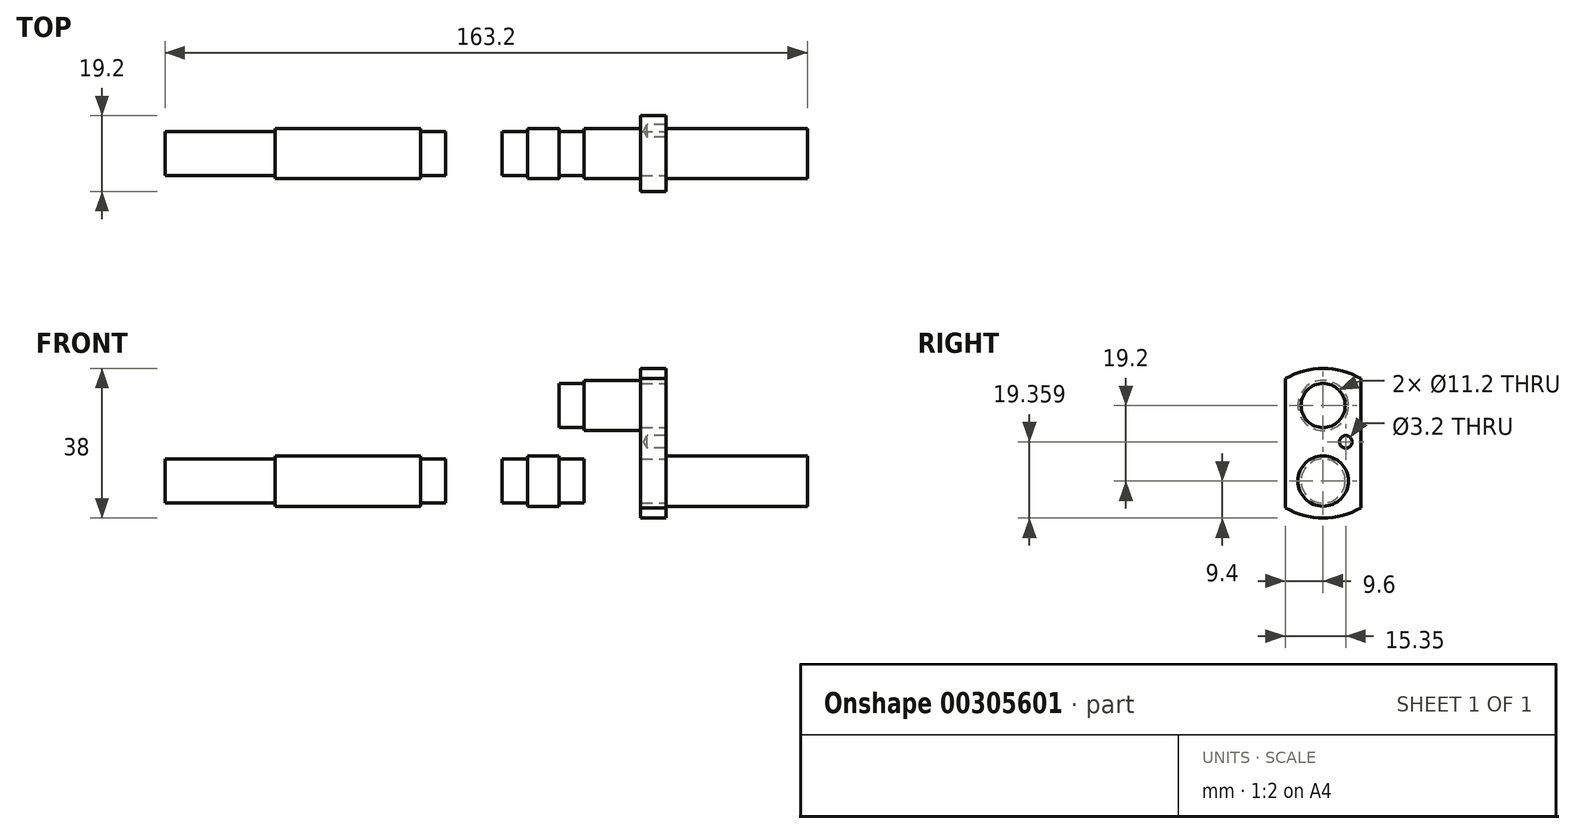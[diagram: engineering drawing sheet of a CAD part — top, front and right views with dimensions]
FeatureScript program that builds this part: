
annotation { "Feature Type Name" : "Feature", "Feature Type Description" : "" }
export const myFeature = defineFeature(function(context is Context, id is Id, definition is map)
    precondition{}
    {
        {
            var Q0;
            Q0=qCreatedBy(makeId("Front.planeOp"),FACE);
            var sketch = newSketch(context, id + "F0", { "sketchPlane" : qUnion([Q0]), "disableImprinting" : false});
            skLineSegment(sketch, "E0", {"start": v(97.03, 0) * mm, "end": v(-113.51, 0) * mm, "construction": true});
            skLineSegment(sketch, "E1", {"start": v(0, 41.9) * mm, "end": v(0, 0) * mm, "construction": true});
            skLineSegment(sketch, "E2", {"start": v(35.2, 41.9) * mm, "end": v(35.2, 0) * mm, "construction": true});
            skLineSegment(sketch, "E3", {"start": v(7.2, 0) * mm, "end": v(7.2, -28.31) * mm, "construction": true});
            skLineSegment(sketch, "E4", {"start": v(13.6, 0) * mm, "end": v(13.6, -28.31) * mm, "construction": true});
            skLineSegment(sketch, "E5", {"start": v(-7.2, 0) * mm, "end": v(-7.2, -28.31) * mm, "construction": true});
            skLineSegment(sketch, "E6", {"start": v(-13.6, 0) * mm, "end": v(-13.6, -28.31) * mm, "construction": true});
            skLineSegment(sketch, "E7", {"start": v(21.6, 0) * mm, "end": v(21.6, -28.31) * mm, "construction": true});
            skLineSegment(sketch, "E8", {"start": v(28, 0) * mm, "end": v(28, -28.31) * mm, "construction": true});
            skLineSegment(sketch, "E9", {"start": v(42.4, 0) * mm, "end": v(42.4, -28.31) * mm, "construction": true});
            skLineSegment(sketch, "E10", {"start": v(42.4, -28.31) * mm, "end": v(48.8, -28.31) * mm, "construction": true});
            skLineSegment(sketch, "E11", {"start": v(48.8, -28.31) * mm, "end": v(48.8, 0) * mm, "construction": true});
            skLineSegment(sketch, "E12", {"start": v(28, -28.31) * mm, "end": v(21.6, -28.31) * mm, "construction": true});
            skLineSegment(sketch, "E13", {"start": v(13.6, -28.31) * mm, "end": v(7.2, -28.31) * mm, "construction": true});
            skLineSegment(sketch, "E14", {"start": v(-7.2, -28.31) * mm, "end": v(-13.6, -28.31) * mm, "construction": true});
            skLineSegment(sketch, "E15", {"start": v(61.58, 19.2) * mm, "end": v(16.8, 19.2) * mm, "construction": true});
            skLineSegment(sketch, "E16", {"start": v(48.8, -6.4) * mm, "end": v(84.7, -6.4) * mm});
            skLineSegment(sketch, "E17", {"start": v(84.7, -6.4) * mm, "end": v(84.7, 0) * mm});
            skLineSegment(sketch, "E18", {"start": v(84.7, 0) * mm, "end": v(42.4, 0) * mm});
            skLineSegment(sketch, "E19", {"start": v(48.8, -6.4) * mm, "end": v(48.8, -5.6) * mm});
            skLineSegment(sketch, "E20", {"start": v(48.8, -5.6) * mm, "end": v(42.4, -5.6) * mm});
            skLineSegment(sketch, "E21", {"start": v(42.4, -5.6) * mm, "end": v(42.4, 0) * mm});
            skLineSegment(sketch, "E22", {"start": v(28, 0) * mm, "end": v(7.2, 0) * mm});
            skLineSegment(sketch, "E23", {"start": v(7.2, -5.6) * mm, "end": v(13.6, -5.6) * mm});
            skLineSegment(sketch, "E24", {"start": v(13.6, -5.6) * mm, "end": v(13.6, -6.4) * mm});
            skLineSegment(sketch, "E25", {"start": v(13.6, -6.4) * mm, "end": v(21.6, -6.4) * mm});
            skLineSegment(sketch, "E26", {"start": v(21.6, -6.4) * mm, "end": v(21.6, -5.6) * mm});
            skLineSegment(sketch, "E27", {"start": v(21.6, -5.6) * mm, "end": v(28, -5.6) * mm});
            skLineSegment(sketch, "E28", {"start": v(28, -5.6) * mm, "end": v(28, 0) * mm});
            skLineSegment(sketch, "E29", {"start": v(7.2, 0) * mm, "end": v(7.2, -5.6) * mm});
            skLineSegment(sketch, "E30", {"start": v(-7.2, 0) * mm, "end": v(-7.2, -5.6) * mm});
            skLineSegment(sketch, "E31", {"start": v(-7.2, -5.6) * mm, "end": v(-13.6, -5.6) * mm});
            skLineSegment(sketch, "E32", {"start": v(-13.6, -5.6) * mm, "end": v(-13.6, -6.4) * mm});
            skLineSegment(sketch, "E33", {"start": v(-13.6, -6.4) * mm, "end": v(-50.5, -6.4) * mm});
            skLineSegment(sketch, "E34", {"start": v(-50.5, -6.4) * mm, "end": v(-50.5, -5.6) * mm});
            skLineSegment(sketch, "E35", {"start": v(-50.5, -5.6) * mm, "end": v(-78.5, -5.6) * mm});
            skLineSegment(sketch, "E36", {"start": v(-78.5, -5.6) * mm, "end": v(-78.5, 0) * mm});
            skLineSegment(sketch, "E37", {"start": v(-78.5, 0) * mm, "end": v(-7.2, 0) * mm});
            skLineSegment(sketch, "E38", {"start": v(48.8, 19.2) * mm, "end": v(48.8, 13.6) * mm});
            skLineSegment(sketch, "E39", {"start": v(48.8, 13.6) * mm, "end": v(42.4, 13.6) * mm});
            skLineSegment(sketch, "E40", {"start": v(42.4, 13.6) * mm, "end": v(42.4, 12.8) * mm});
            skLineSegment(sketch, "E41", {"start": v(42.4, 12.8) * mm, "end": v(28, 12.8) * mm});
            skLineSegment(sketch, "E42", {"start": v(28, 12.8) * mm, "end": v(28, 13.6) * mm});
            skLineSegment(sketch, "E43", {"start": v(28, 13.6) * mm, "end": v(21.6, 13.6) * mm});
            skLineSegment(sketch, "E44", {"start": v(21.6, 13.6) * mm, "end": v(21.6, 19.2) * mm});
            skLineSegment(sketch, "E45", {"start": v(21.6, 19.2) * mm, "end": v(48.8, 19.2) * mm});
            skSolve(sketch);
        }
        {
            var Q0;
            Q0=makeQuery(id+"F0.imprint","IMPRINT",FACE,{"disambiguationData":[TD([[makeQuery(id+"F0.imprint","IMPRINT",EDGE,{"derivedFrom":sQuery(id+"F0.wireOp",EDGE,"E16")}),1.0]])]});
            var Q1;
            Q1=makeQuery(id+"F0.imprint","IMPRINT",FACE,{"disambiguationData":[TD([[makeQuery(id+"F0.imprint","IMPRINT",EDGE,{"derivedFrom":sQuery(id+"F0.wireOp",EDGE,"E22")}),1.0]])]});
            var Q2;
            Q2=makeQuery(id+"F0.imprint","IMPRINT",FACE,{"disambiguationData":[TD([[makeQuery(id+"F0.imprint","IMPRINT",EDGE,{"derivedFrom":sQuery(id+"F0.wireOp",EDGE,"E30")}),-1.0]])]});
            var Q3;
            Q3=sQuery(id+"F0.wireOp",EDGE,"E0");
            revolve(context, id + "F1", {"surfaceOperationType" : NewSurfaceOperationType.NEW, "entities" : qUnion([Q0, Q1, Q2]), "axis" : qUnion([Q3]), "revolveType" : RevolveType.FULL});
        }
        {
            var Q0;
            Q0=makeQuery(id+"F0.imprint","IMPRINT",FACE,{"disambiguationData":[TD([[makeQuery(id+"F0.imprint","IMPRINT",EDGE,{"derivedFrom":sQuery(id+"F0.wireOp",EDGE,"E38")}),-1.0]])]});
            var Q1;
            Q1=sQuery(id+"F0.wireOp",EDGE,"E15");
            revolve(context, id + "F2", {"surfaceOperationType" : NewSurfaceOperationType.NEW, "entities" : qUnion([Q0]), "axis" : qUnion([Q1]), "revolveType" : RevolveType.FULL});
        }
        {
            var Q0;
            Q0=makeQuery(id+"F2.opRevolve","SWEPT_FACE",FACE,{"disambiguationData":[OSD([sQuery(id+"F0.wireOp",EDGE,"E38")])]});
            var sketch = newSketch(context, id + "F3", { "sketchPlane" : qUnion([Q0]), "disableImprinting" : false});
            skCircle(sketch, "E46", {"center": v(0, 19.2) * mm, "radius": 5.6 * mm});
            skCircle(sketch, "E47", {"center": v(0, 0) * mm, "radius": 5.6 * mm});
            skArc(sketch, "E48", {"start": v(-9.6, -6.8) * mm, "mid": v(0, -9.4) * mm, "end": v(9.6, -6.8) * mm});
            skLineSegment(sketch, "E49", {"start": v(10.66, 19.2) * mm, "end": v(0, 19.2) * mm, "construction": true});
            skLineSegment(sketch, "E50", {"start": v(0, 0) * mm, "end": v(12.05, 0) * mm, "construction": true});
            skLineSegment(sketch, "E51", {"start": v(0, 9.6) * mm, "end": v(10.74, 9.6) * mm, "construction": true});
            skLineSegment(sketch, "E52.left", {"start": v(9.6, 26) * mm, "end": v(9.6, -6.8) * mm});
            skLineSegment(sketch, "E52.right", {"start": v(-9.6, 26) * mm, "end": v(-9.6, -6.8) * mm});
            skArc(sketch, "E53.trimOffspring", {"start": v(9.6, 26) * mm, "mid": v(0, 28.6) * mm, "end": v(-9.6, 26) * mm});
            skPoint(sketch, "E54", {"position": v(5.75, 9.96) * mm});
            skCircle(sketch, "E55", {"center": v(0, 0) * mm, "radius": 11.5 * mm, "construction": true});
            skLineSegment(sketch, "E56", {"start": v(5.75, 9.96) * mm, "end": v(0, 0) * mm, "construction": true});
            skSolve(sketch);
        }
        {
            var Q0;
            Q0=makeQuery(id+"F3.imprint","IMPRINT",FACE,{"disambiguationData":[TD([[makeQuery(id+"F3.imprint","IMPRINT",EDGE,{"derivedFrom":sQuery(id+"F3.wireOp",EDGE,"E46")}),-1.0]])]});
            extrude(context, id + "F4", {"entities" : qUnion([Q0]), "oppositeDirection" : true, "depth" : 6.4 * mm, "offsetDistance" : 25 * mm});
        }
        {
            var Q0;
            Q0=sQuery(id+"F3.wireOp",VERTEX,"E54");
            var Q1;
            Q1=makeQuery(id+"F4.opExtrude","SWEPT_BODY",BODY,{"disambiguationData":[OSD([sQuery(id+"F3.wireOp",EDGE,"E46"),sQuery(id+"F3.wireOp",EDGE,"E47"),sQuery(id+"F3.wireOp",EDGE,"E48"),sQuery(id+"F3.wireOp",EDGE,"E52.left"),sQuery(id+"F3.wireOp",EDGE,"E52.right"),sQuery(id+"F3.wireOp",EDGE,"E53.trimOffspring")])]});
            hole(context, id + "F5", {"style" : HoleStyle.SIMPLE, "endStyle" : HoleEndStyle.BLIND, "holeDiameter" : 3.2 * mm, "majorDiameter" : 4 * mm, "holeDepth" : 4.8 * mm, "tappedDepth" : 5.9 * mm, "tapClearance" : 2, "locations" : qUnion([Q0]), "scope" : qUnion([Q1]), "startStyle" : HoleStartStyle.PART});
        }
    });
